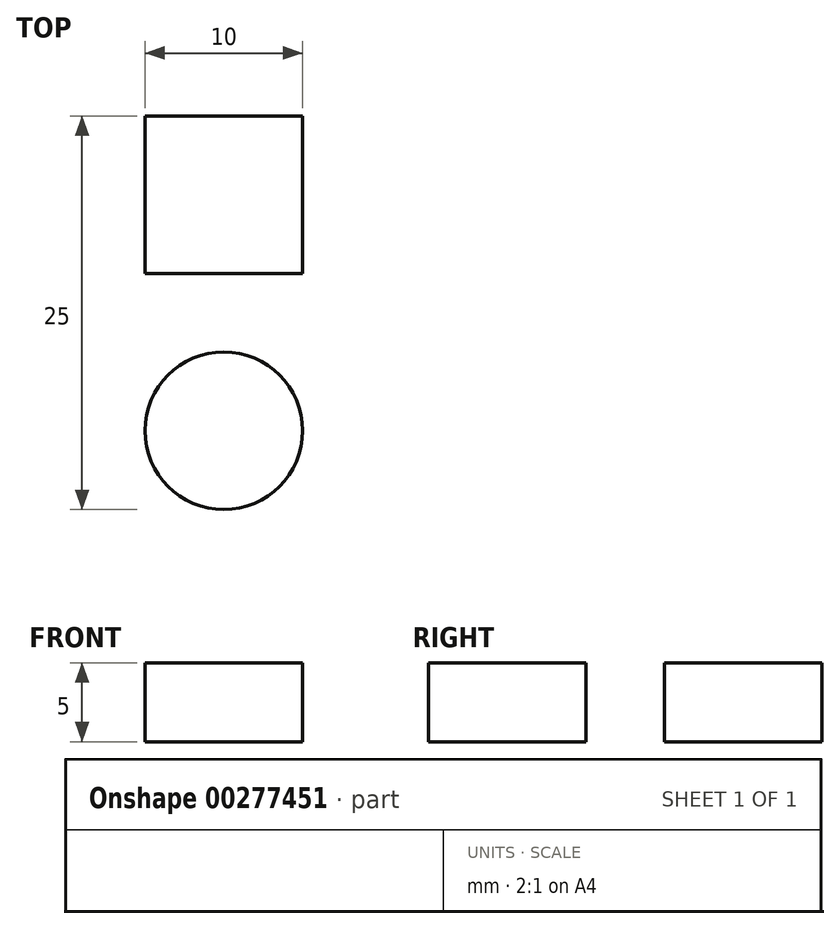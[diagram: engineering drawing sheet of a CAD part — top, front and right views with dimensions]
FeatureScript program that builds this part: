
annotation { "Feature Type Name" : "Feature", "Feature Type Description" : "" }
export const myFeature = defineFeature(function(context is Context, id is Id, definition is map)
    precondition{}
    {
        {
            var Q0;
            Q0=qCreatedBy(makeId("Top.planeOp"),FACE);
            var sketch = newSketch(context, id + "F0", { "sketchPlane" : qUnion([Q0])});
            skLineSegment(sketch, "E0.bottom", {"start": v(5, 5) * mm, "end": v(-5, 5) * mm});
            skLineSegment(sketch, "E0.top", {"start": v(5, -5) * mm, "end": v(-5, -5) * mm});
            skLineSegment(sketch, "E0.left", {"start": v(5, 5) * mm, "end": v(5, -5) * mm});
            skLineSegment(sketch, "E0.right", {"start": v(-5, 5) * mm, "end": v(-5, -5) * mm});
            skPoint(sketch, "E0.middle", {"position": v(0, 0) * mm});
            skCircle(sketch, "E1", {"center": v(0, -15) * mm, "radius": 5 * mm});
            skSolve(sketch);
        }
        {
            var Q0;
            Q0=makeQuery(id+"F0.imprint","IMPRINT",FACE,{"disambiguationData":[TD([[makeQuery(id+"F0.imprint","IMPRINT",EDGE,{"derivedFrom":sQuery(id+"F0.wireOp",EDGE,"E0.bottom")}),1.0]])]});
            var Q1;
            Q1=makeQuery(id+"F0.imprint","IMPRINT",FACE,{"disambiguationData":[TD([[makeQuery(id+"F0.imprint","IMPRINT",EDGE,{"derivedFrom":sQuery(id+"F0.wireOp",EDGE,"E1")}),1.0]])]});
            extrude(context, id + "F1", {"entities" : qUnion([Q0, Q1]), "depth" : 5 * mm});
        }
    });
